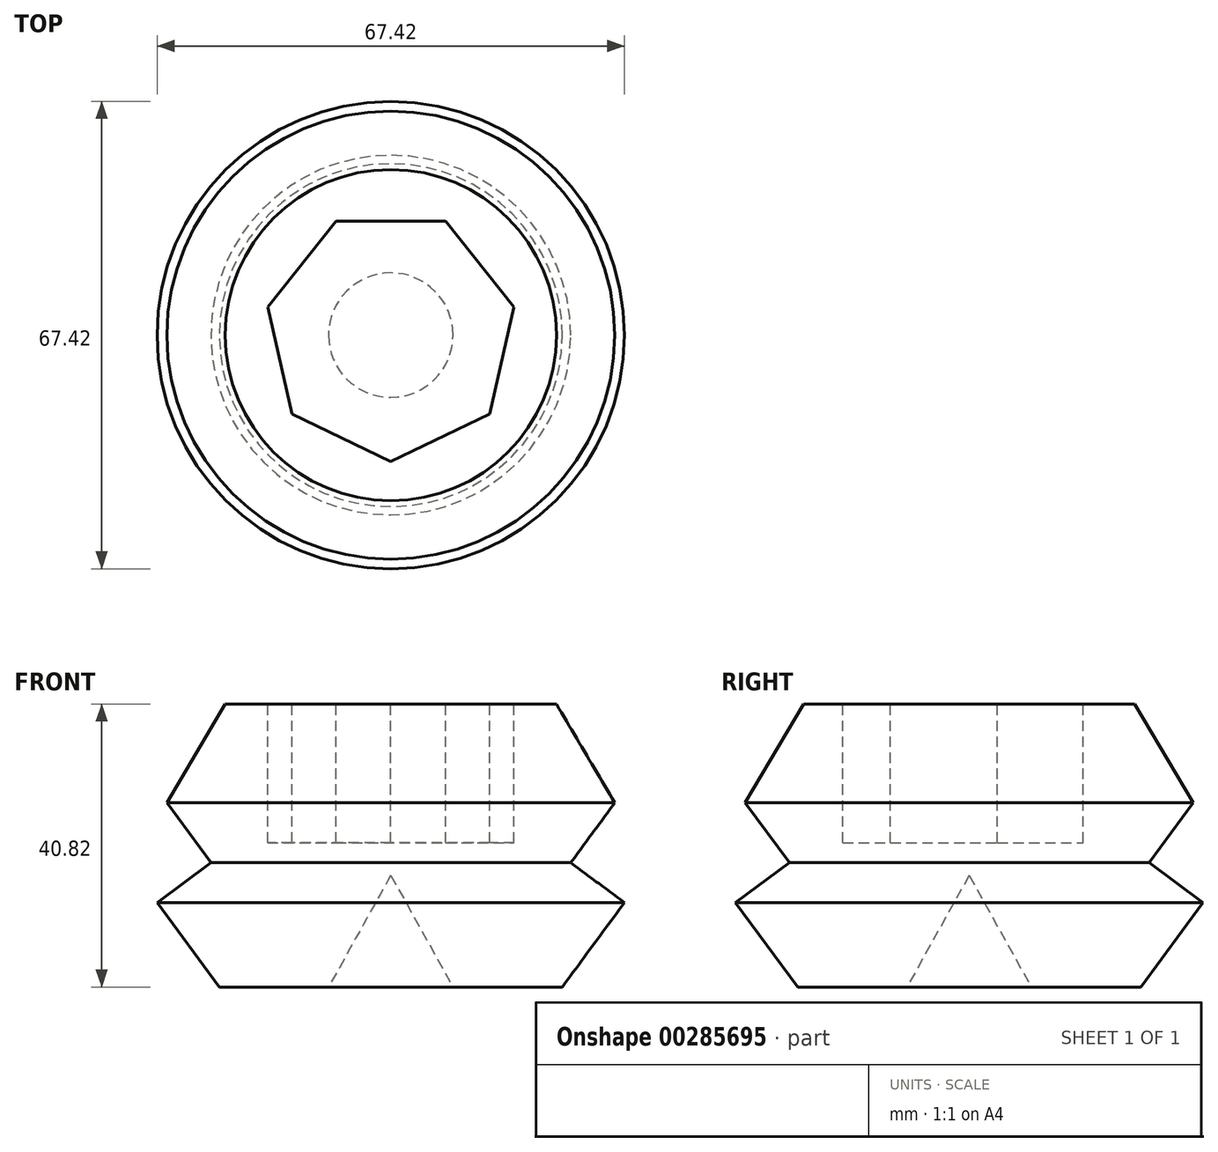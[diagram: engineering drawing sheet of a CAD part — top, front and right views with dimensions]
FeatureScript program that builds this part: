
annotation { "Feature Type Name" : "Feature", "Feature Type Description" : "" }
export const myFeature = defineFeature(function(context is Context, id is Id, definition is map)
    precondition{}
    {
        {
            var Q0;
            Q0=qCreatedBy(makeId("Front.planeOp"),FACE);
            var sketch = newSketch(context, id + "F0", { "sketchPlane" : qUnion([Q0])});
            skLineSegment(sketch, "E0", {"start": v(0, 16.1) * mm, "end": v(-8.98, 0) * mm});
            skLineSegment(sketch, "E1", {"start": v(-8.98, 0) * mm, "end": v(-24.73, 0) * mm});
            skLineSegment(sketch, "E2", {"start": v(-24.73, 0) * mm, "end": v(-33.7, 12.2) * mm});
            skLineSegment(sketch, "E3", {"start": v(-33.7, 12.2) * mm, "end": v(-25.94, 17.92) * mm});
            skLineSegment(sketch, "E4", {"start": v(-25.94, 17.92) * mm, "end": v(-32.3, 26.57) * mm});
            skLineSegment(sketch, "E5", {"start": v(-32.3, 26.57) * mm, "end": v(-23.88, 40.82) * mm});
            skLineSegment(sketch, "E6", {"start": v(-23.88, 40.82) * mm, "end": v(0, 40.82) * mm});
            skLineSegment(sketch, "E7", {"start": v(0, 40.82) * mm, "end": v(0, 16.1) * mm});
            skSolve(sketch);
        }
        {
            var Q0;
            Q0 = qSketchRegion(id + "F0", true);
            var Q1;
            Q1=sQuery(id+"F0.wireOp",EDGE,"E7");
            revolve(context, id + "F1", {"entities" : qUnion([Q0]), "axis" : qUnion([Q1]), "revolveType" : RevolveType.FULL});
        }
        {
            var Q0;
            Q0=makeQuery(id+"F1.opRevolve","SWEPT_FACE",FACE,{"disambiguationData":[OSD([sQuery(id+"F0.wireOp",EDGE,"E6")])]});
            var sketch = newSketch(context, id + "F2", { "sketchPlane" : qUnion([Q0])});
            skCircle(sketch, "E8.cCircle", {"center": v(0, 0) * mm, "radius": 16.42 * mm, "construction": true});
            skLineSegment(sketch, "E8.0", {"start": v(-7.9, 16.42) * mm, "end": v(7.9, 16.42) * mm});
            skLineSegment(sketch, "E8.1", {"start": v(7.9, 16.42) * mm, "end": v(17.77, 4.06) * mm});
            skLineSegment(sketch, "E8.2", {"start": v(17.77, 4.06) * mm, "end": v(14.25, -11.36) * mm});
            skLineSegment(sketch, "E8.3", {"start": v(14.25, -11.36) * mm, "end": v(0, -18.22) * mm});
            skLineSegment(sketch, "E8.4", {"start": v(0, -18.22) * mm, "end": v(-14.25, -11.36) * mm});
            skLineSegment(sketch, "E8.5", {"start": v(-14.25, -11.36) * mm, "end": v(-17.77, 4.06) * mm});
            skLineSegment(sketch, "E8.6", {"start": v(-17.77, 4.06) * mm, "end": v(-7.9, 16.42) * mm});
            skPoint(sketch, "E8.0.midPoint", {"position": v(0, 16.42) * mm});
            skSolve(sketch);
        }
        {
            var Q0;
            Q0=makeQuery(id+"F2.imprint","IMPRINT",FACE,{"disambiguationData":[TD([[makeQuery(id+"F2.imprint","IMPRINT",EDGE,{"derivedFrom":sQuery(id+"F2.wireOp",EDGE,"E8.0")}),-1.0]])]});
            var Q1;
            Q1 = qSketchRegion(id + "F2", true);
            extrude(context, id + "F3", {"entities" : qUnion([Q0, Q1]), "operationType" : NewBodyOperationType.REMOVE, "oppositeDirection" : true, "depth" : 20 * mm});
        }
    });
